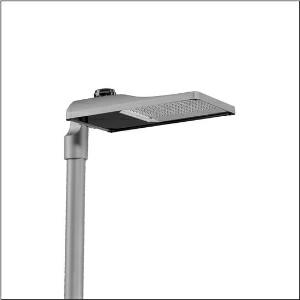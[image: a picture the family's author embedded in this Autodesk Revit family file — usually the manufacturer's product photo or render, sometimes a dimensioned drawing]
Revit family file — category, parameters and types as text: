
# Revit family: streetlight_sl_31_maxi___pl52_5xh8h75n08sa_385d
name_source: partatom
category: Lighting Fixtures
units: mm (PartAtom-declared; Revit-internal decimal feet)

## family parameters
Cut with Voids When Loaded = No
Host = Face
Light Source = No
Part Type = Normal
Room Calculation Point = No
Round Connector Dimension = Use Diameter
Shared = No

## types (1)
- --- (1 x LED, 22470 lm, 208.6 W, 2200K)
    Apparent Load = 209 VA
    CIE Flux Codes = 27 59 98 100 100
    Color Rendering = 70
    Color Temperature = 2200K
    Default Elevation = 1800 mm
    Description = Streetlight SL 31 maxi NEMA (7pin), Desk-Remote mast luminaire for post-top, side-entry; light control with lens of PMMA; light distribution: PL52, direct asymmetric distribution, for standard-compliant lighting for roads and squares; LED: luminous flux: 22.470lm, light colour: 722, colour temperature: 2200K; luminous efficacy: 107,7lm/W; control: pre-setting: linear dimming characteristic, flexible luminous flux parameterisation, time-dependent luminous flux control, constant luminous flux control, intelligent temperature release in ECG and LED module, overheat protection; luminaire housing, of diecast aluminium, Siteco® metallic grey (DB 702S), corrosivity category C5 high according to DIN EN ISO 12944; cover of toughened safety glass, transparent, opened without tools; mast flange of diecast aluminium, Siteco® metallic grey (DB 702S), spigot size: 76/60mm, mast flange included unmounted; with cable H07RN-F 3x 1.5mm², cable length: 14,5m, connection cable pre-assembled; mains connection: 220..240V, AC, 50/60Hz; power consumption (at start of service life): 208,6W / (at end of service life): 233,1W / (with reduced operation 50%): 88W; protection rating (complete): IP66; insulation class (complete): insulation class I (protective earthing); impact resistance: IK09; certification: CE, ENEC, ENEC+, VDE, UKCA; permissible operating ambient temperature for outdoor applications: -40..+50°C; packaging unit: 1 piece

Light Distribution: PL52
    Height = 79 mm
    Lamp = 1 x LED
    Lamp Light Flux = 22470 lm
    Lamp Power = 208.6 W
    Lamp count = 1
    Length = 657 mm
    Luminous efficacy = 108 lm/W
    Manufacturer = Siteco
    ModVariant = No
    Model = 5XH8H75N08SA
    Number of Poles = 1
    OnlyDefault = Yes
    Power Factor = 1
    Product Name = Streetlight SL 31 maxi | PL52
    Product group = mast luminaire | pylon top
    ProductGroupID = 6100
    Protection Class = Protection class I
    Protection Degree = IP 66
    RLX_Detail_Level = 1
    RLX_Emergency_Light_Flux = 0 lm
    RLX_Emergency_Type = 0
    RLX_Emergency_Type_DB = No
    RlxData = <blob elided: 56921 chars, md5=3edd7596>
    Socket = socket
    Standby Power = 0 W
    System Light Flux = 22470 lm
    System Power = 209 W
    Type Comments = factory setting: luminous flux: 100 % | dim-lin: 254 | 718 mA
    Type Image = l_1300293.jpg
    URL = http://relux.com
    VarID = @adj_007937
    Voltage = 0 V
    Weight = 0.00 kg
    Width = 362 mm

## geometry (parser evidence)
native form markers: Blend x4, Sweep x10
no freeform markers — native parametric forms only
